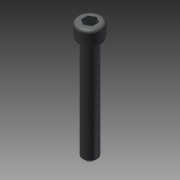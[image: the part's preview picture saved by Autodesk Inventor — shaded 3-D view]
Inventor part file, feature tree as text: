
AUTODESK INVENTOR PART (.ipt)
format: ipt  version: 2015 (Build 190159000, 159)  size: 115,712 bytes
history: native  units: in
note: dims shown in document units (in); Inventor stores cm internally (conversion verified against a paired STEP export)
features: other x6, extrude x1, chamfer x1, sketch x1
ambient origin geometry x8: Origin, YZ Plane, XZ Plane, XY Plane, X Axis, Y Axis, Z Axis, Center Point
bodies: Solid1 (feature_tree)
feature tree (9):
  other  "Screw 1.5in - 739195.ipt"
  extrude  "Extrusion1"  Depth=0.5in TaperAngle=0.0deg
  chamfer  "Chamfer1"  Distance=0.035in Angle=45.0deg
  other  "tetrix_739195_2013::Screw 1.5in - 739195.ipt"
  other  "TaggingFeature1"
  other  "FRONT"
  other  "TOP"
  other  "RIGHT"
  sketch  "Sketch1"  dims[d0=0.3937in d1=0.5in d2=0.0in d3=0.035in d4=0.125in d5=45.0deg]
